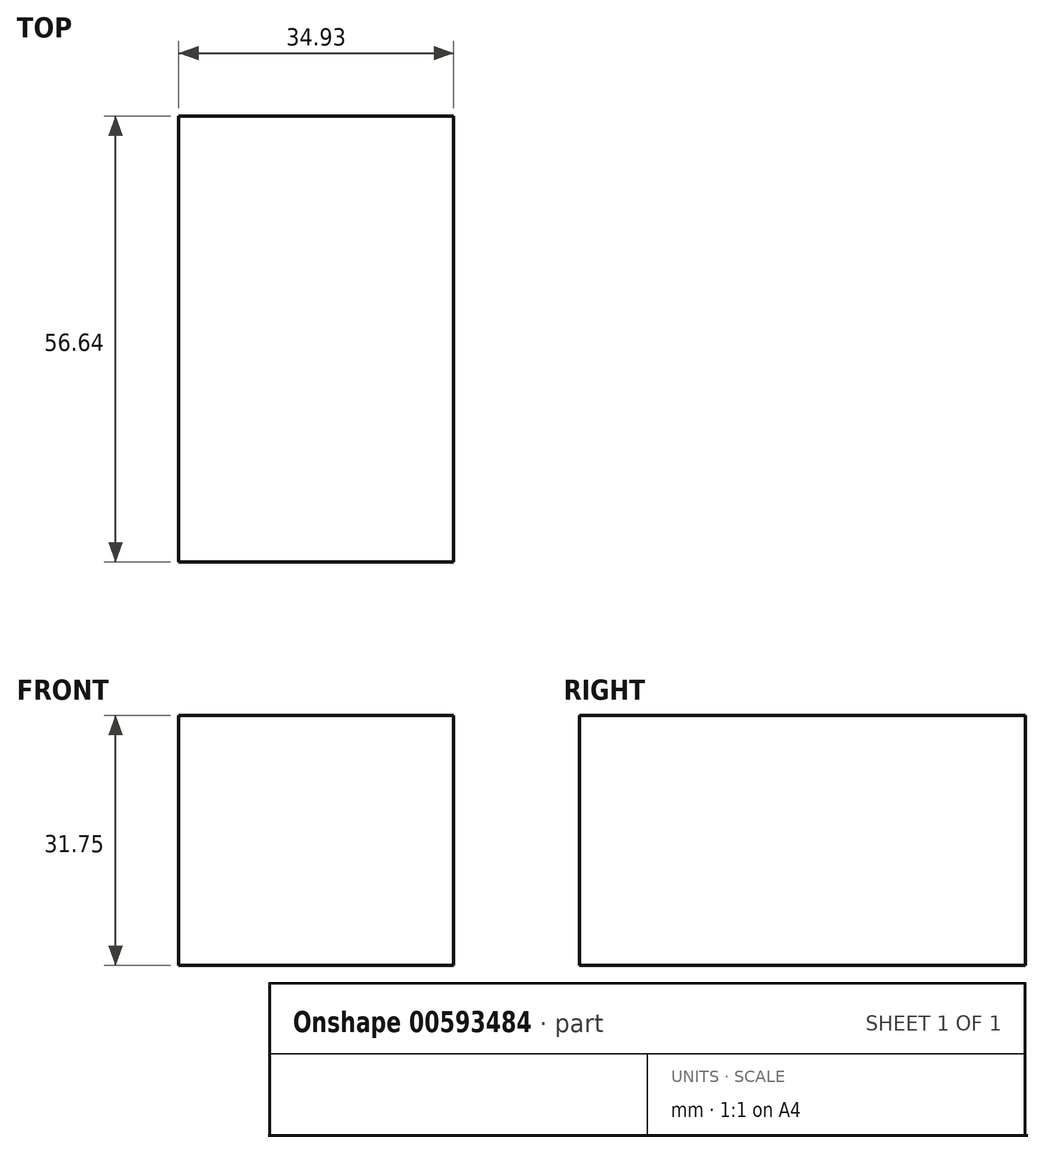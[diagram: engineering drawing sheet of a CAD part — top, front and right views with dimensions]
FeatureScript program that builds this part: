
annotation { "Feature Type Name" : "Feature", "Feature Type Description" : "" }
export const myFeature = defineFeature(function(context is Context, id is Id, definition is map)
    precondition{}
    {
        {
            var Q0;
            Q0=qCreatedBy(makeId("Front.planeOp"),FACE);
            var sketch = newSketch(context, id + "F0", { "sketchPlane" : qUnion([Q0])});
            skLineSegment(sketch, "E0.bottom", {"start": v(4.36, 12.04) * mm, "end": v(39.29, 12.04) * mm});
            skLineSegment(sketch, "E0.top", {"start": v(4.36, -19.71) * mm, "end": v(39.29, -19.71) * mm});
            skLineSegment(sketch, "E0.left", {"start": v(4.36, 12.04) * mm, "end": v(4.36, -19.71) * mm});
            skLineSegment(sketch, "E0.right", {"start": v(39.29, 12.04) * mm, "end": v(39.29, -19.71) * mm});
            skLineSegment(sketch, "E1.bottom", {"start": v(39.29, 12.04) * mm, "end": v(21.82, 12.04) * mm});
            skSolve(sketch);
        }
        {
            var Q0;
            Q0 = qSketchRegion(id + "F0", true);
            extrude(context, id + "F1", {"entities" : qUnion([Q0]), "depth" : 56.64 * mm, "offsetDistance" : 25.4 * mm});
        }
        {
            var Q0;
            Q0=qCreatedBy(makeId("Right.planeOp"),FACE);
            cPlane(context, id + "F2", {"entities" : qUnion([Q0]), "cplaneType" : CPlaneType.OFFSET, "offset" : 21.8 * mm, "width" : 152.4 * mm, "height" : 152.4 * mm});
        }
    });
